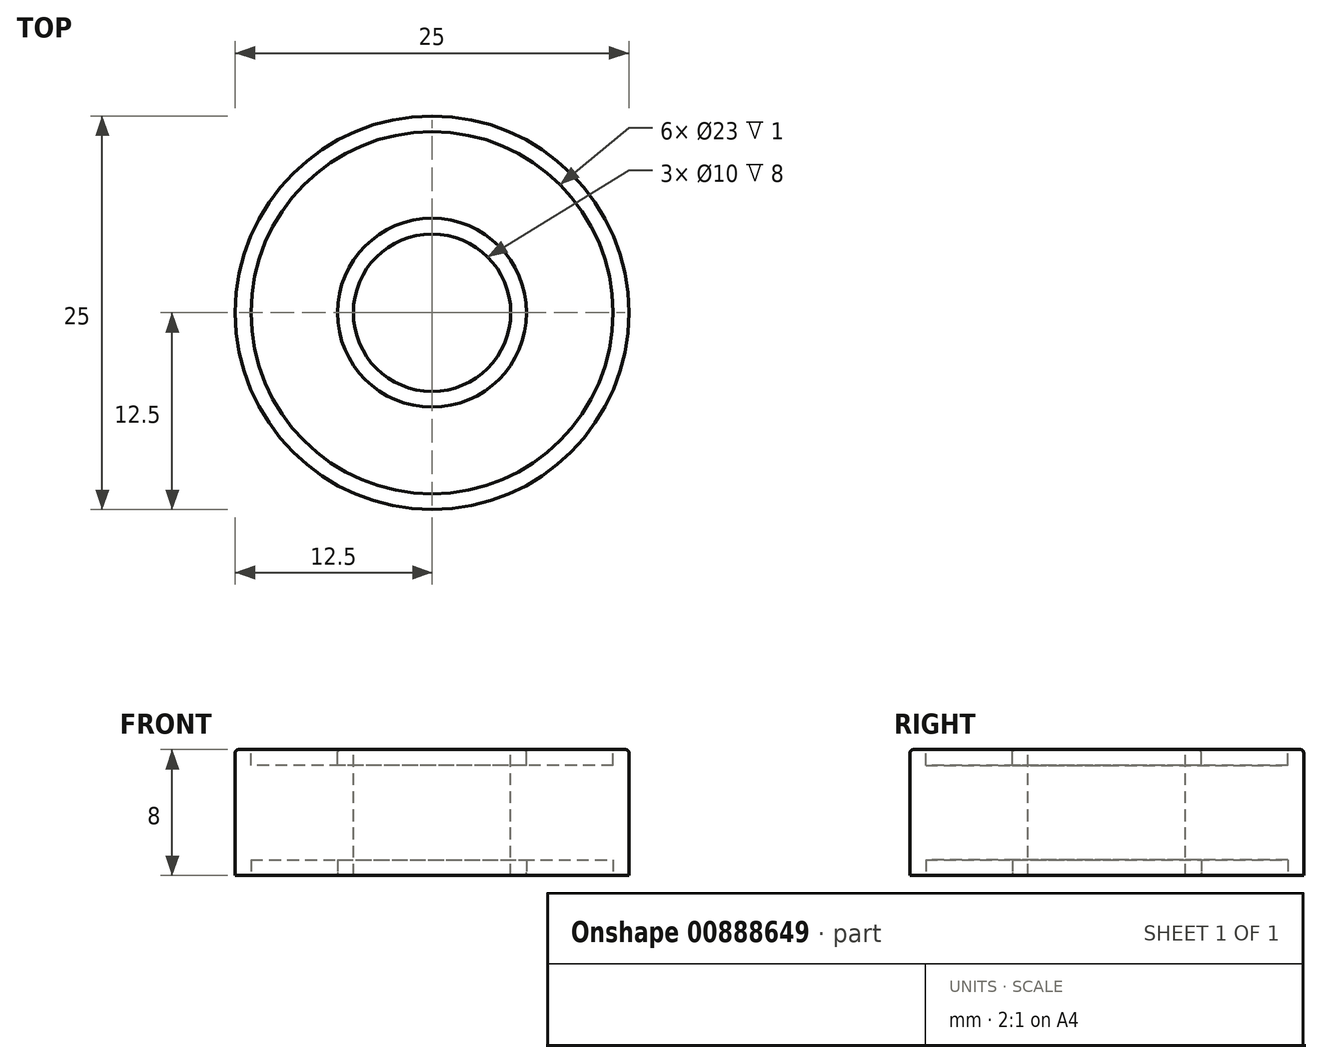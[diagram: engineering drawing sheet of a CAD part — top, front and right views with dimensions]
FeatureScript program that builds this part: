
annotation { "Feature Type Name" : "Feature", "Feature Type Description" : "" }
export const myFeature = defineFeature(function(context is Context, id is Id, definition is map)
    precondition{}
    {
        {
            var Q0;
            Q0=qCreatedBy(makeId("Top.planeOp"),FACE);
            var sketch = newSketch(context, id + "F0", { "sketchPlane" : qUnion([Q0])});
            skCircle(sketch, "E0", {"center": v(0, 0) * mm, "radius": 12.5 * mm});
            skSolve(sketch);
        }
        {
            var Q0;
            Q0=makeQuery(id+"F0.imprint","IMPRINT",FACE,{"disambiguationData":[TD([[makeQuery(id+"F0.imprint","IMPRINT",EDGE,{"derivedFrom":sQuery(id+"F0.wireOp",EDGE,"E0")}),1.0]])]});
            extrude(context, id + "F1", {"entities" : qUnion([Q0]), "depth" : 8 * mm, "offsetDistance" : 25.4 * mm});
        }
        {
            var Q0;
            Q0=makeQuery(id+"F1.opExtrude","CAP_FACE",FACE,{"disambiguationData":[OSD([sQuery(id+"F0.wireOp",EDGE,"E0")])],"isStart":false});
            var sketch = newSketch(context, id + "F2", { "sketchPlane" : qUnion([Q0])});
            skCircle(sketch, "E1", {"center": v(0, 0) * mm, "radius": 5 * mm});
            skSolve(sketch);
        }
        {
            var Q0;
            Q0=makeQuery(id+"F2.imprint","IMPRINT",FACE,{"disambiguationData":[TD([[makeQuery(id+"F2.imprint","IMPRINT",EDGE,{"derivedFrom":sQuery(id+"F2.wireOp",EDGE,"E1")}),1.0]])]});
            extrude(context, id + "F3", {"entities" : qUnion([Q0]), "operationType" : NewBodyOperationType.REMOVE, "endBound" : BoundingType.THROUGH_ALL, "oppositeDirection" : true, "depth" : 25.4 * mm, "offsetDistance" : 25.4 * mm});
        }
        {
            var Q0;
            Q0=makeQuery(id+"F1.opExtrude","CAP_FACE",FACE,{"disambiguationData":[OSD([sQuery(id+"F0.wireOp",EDGE,"E0")])],"isStart":false});
            var sketch = newSketch(context, id + "F4", { "sketchPlane" : qUnion([Q0])});
            skCircle(sketch, "E2", {"center": v(0, 0) * mm, "radius": 6 * mm});
            skCircle(sketch, "E3", {"center": v(0, 0) * mm, "radius": 11.5 * mm});
            skSolve(sketch);
        }
        {
            var Q0;
            Q0 = qSketchRegion(id + "F4", true);
            extrude(context, id + "F5", {"entities" : qUnion([Q0]), "operationType" : NewBodyOperationType.REMOVE, "oppositeDirection" : true, "depth" : 1 * mm, "offsetDistance" : 25.4 * mm});
        }
        {
            var Q0;
            Q0=makeQuery(id+"F1.opExtrude","CAP_FACE",FACE,{"disambiguationData":[OSD([sQuery(id+"F0.wireOp",EDGE,"E0")])],"isStart":true});
            var sketch = newSketch(context, id + "F6", { "sketchPlane" : qUnion([Q0])});
            skCircle(sketch, "E4", {"center": v(0, 0) * mm, "radius": 6 * mm});
            skCircle(sketch, "E5", {"center": v(0, 0) * mm, "radius": 11.5 * mm});
            skSolve(sketch);
        }
        {
            var Q0;
            Q0 = qSketchRegion(id + "F6", true);
            extrude(context, id + "F7", {"entities" : qUnion([Q0]), "operationType" : NewBodyOperationType.REMOVE, "oppositeDirection" : true, "depth" : 1 * mm, "offsetDistance" : 25.4 * mm});
        }
        {
            var Q0;
            Q0=makeQuery(id+"F1.opExtrude","CAP_EDGE",EDGE,{"disambiguationData":[OSD([sQuery(id+"F0.wireOp",EDGE,"E0")])],"isStart":false});
            var Q1;
            Q1=makeQuery(id+"F5.boolean.opBoolean","COPY",EDGE,{"derivedFrom":makeQuery(id+"F5.opExtrude","CAP_EDGE",EDGE,{"disambiguationData":[OSD([sQuery(id+"F4.wireOp",EDGE,"E2")])],"isStart":true})});
            var Q2;
            Q2=makeQuery(id+"F7.boolean.opBoolean","COPY",EDGE,{"derivedFrom":makeQuery(id+"F7.opExtrude","CAP_EDGE",EDGE,{"disambiguationData":[OSD([sQuery(id+"F6.wireOp",EDGE,"E4")])],"isStart":true})});
            fillet(context, id + "F8", {"entities" : qUnion([Q0, Q1, Q2]), "radius" : 0.2 * mm, "tangentPropagation" : true, "allowEdgeOverflow" : false});
        }
    });
